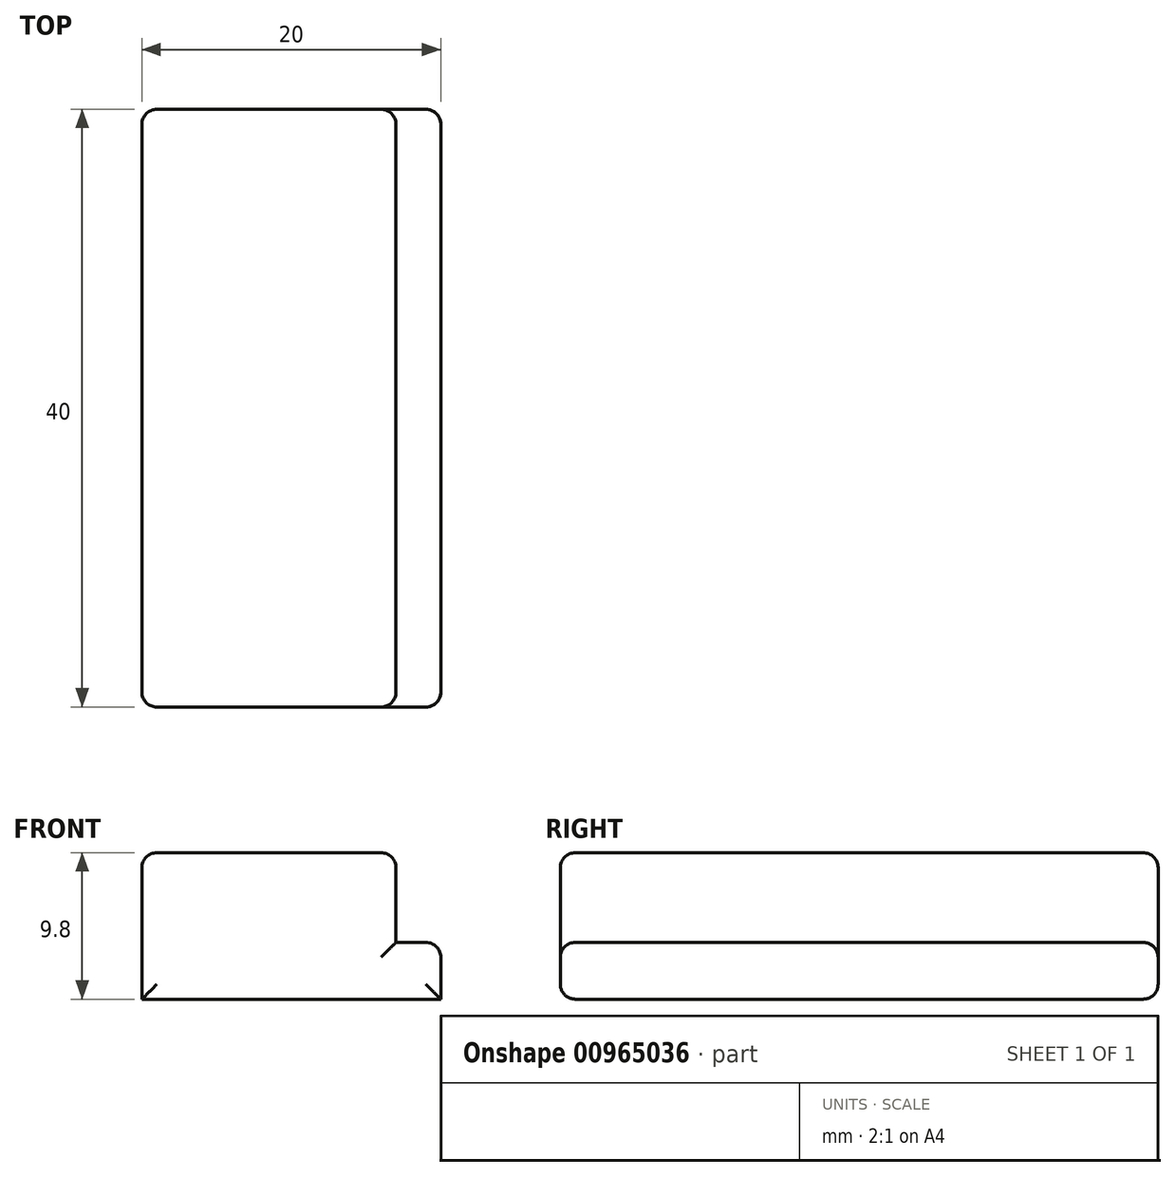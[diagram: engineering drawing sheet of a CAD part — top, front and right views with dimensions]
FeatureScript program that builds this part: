
annotation { "Feature Type Name" : "Feature", "Feature Type Description" : "" }
export const myFeature = defineFeature(function(context is Context, id is Id, definition is map)
    precondition{}
    {
        {
            var Q0;
            Q0=qCreatedBy(makeId("Top.planeOp"),FACE);
            var sketch = newSketch(context, id + "F0", { "sketchPlane" : qUnion([Q0])});
            skLineSegment(sketch, "E0.bottom", {"start": v(-10.66, 24) * mm, "end": v(9.34, 24) * mm});
            skLineSegment(sketch, "E0.top", {"start": v(-10.66, -16) * mm, "end": v(9.34, -16) * mm});
            skLineSegment(sketch, "E0.left", {"start": v(-10.66, 24) * mm, "end": v(-10.66, -16) * mm});
            skLineSegment(sketch, "E0.right", {"start": v(9.34, 24) * mm, "end": v(9.34, -16) * mm});
            skSolve(sketch);
        }
        {
            var Q0;
            Q0 = qSketchRegion(id + "F0", true);
            extrude(context, id + "F1", {"entities" : qUnion([Q0]), "depth" : 3.8 * mm, "offsetDistance" : 25 * mm});
        }
        {
            var Q0;
            Q0=makeQuery(id+"F1.opExtrude","CAP_FACE",FACE,{"disambiguationData":[OSD([sQuery(id+"F0.wireOp",EDGE,"E0.bottom"),sQuery(id+"F0.wireOp",EDGE,"E0.top"),sQuery(id+"F0.wireOp",EDGE,"E0.left"),sQuery(id+"F0.wireOp",EDGE,"E0.right")])],"isStart":false});
            var sketch = newSketch(context, id + "F2", { "sketchPlane" : qUnion([Q0])});
            skLineSegment(sketch, "E1.bottom", {"start": v(-10.66, 24) * mm, "end": v(6.34, 24) * mm});
            skLineSegment(sketch, "E1.top", {"start": v(-10.66, -16) * mm, "end": v(6.34, -16) * mm});
            skLineSegment(sketch, "E1.left", {"start": v(-10.66, 24) * mm, "end": v(-10.66, -16) * mm});
            skLineSegment(sketch, "E1.right", {"start": v(6.34, 24) * mm, "end": v(6.34, -16) * mm});
            skSolve(sketch);
        }
        {
            var Q0;
            Q0 = qSketchRegion(id + "F2", true);
            extrude(context, id + "F3", {"entities" : qUnion([Q0]), "operationType" : NewBodyOperationType.ADD, "depth" : 6 * mm, "offsetDistance" : 25 * mm});
        }
        {
            var Q0;
            Q0=makeQuery(id+"F3.opExtrude","CAP_EDGE",EDGE,{"disambiguationData":[OSD([sQuery(id+"F2.wireOp",EDGE,"E1.right")])],"isStart":false});
            var Q1;
            Q1=makeQuery(id+"F3.opExtrude","CAP_EDGE",EDGE,{"disambiguationData":[OSD([sQuery(id+"F2.wireOp",EDGE,"E1.left")])],"isStart":false});
            var Q2;
            Q2=makeQuery(id+"F1.opExtrude","CAP_EDGE",EDGE,{"disambiguationData":[OSD([sQuery(id+"F0.wireOp",EDGE,"E0.right")])],"isStart":false});
            var Q3;
            Q3=makeQuery(id+"F3.opExtrude","CAP_EDGE",EDGE,{"disambiguationData":[OSD([sQuery(id+"F2.wireOp",EDGE,"E1.bottom")])],"isStart":false});
            var Q4;
            Q4=makeQuery(id+"F3.boolean.opBoolean","MERGE",FACE,{"derivedFrom":[makeQuery(id+"F1.opExtrude","SWEPT_FACE",FACE,{"disambiguationData":[OSD([sQuery(id+"F0.wireOp",EDGE,"E0.bottom")])]}),makeQuery(id+"F3.opExtrude","SWEPT_FACE",FACE,{"disambiguationData":[OSD([sQuery(id+"F2.wireOp",EDGE,"E1.bottom")])]})]});
            var Q5;
            Q5=makeQuery(id+"F3.boolean.opBoolean","MERGE",FACE,{"derivedFrom":[makeQuery(id+"F1.opExtrude","SWEPT_FACE",FACE,{"disambiguationData":[OSD([sQuery(id+"F0.wireOp",EDGE,"E0.top")])]}),makeQuery(id+"F3.opExtrude","SWEPT_FACE",FACE,{"disambiguationData":[OSD([sQuery(id+"F2.wireOp",EDGE,"E1.top")])]})]});
            fillet(context, id + "F4", {"entities" : qUnion([Q0, Q1, Q2, Q3, Q4, Q5]), "radius" : 1 * mm, "tangentPropagation" : true, "allowEdgeOverflow" : false});
        }
    });
